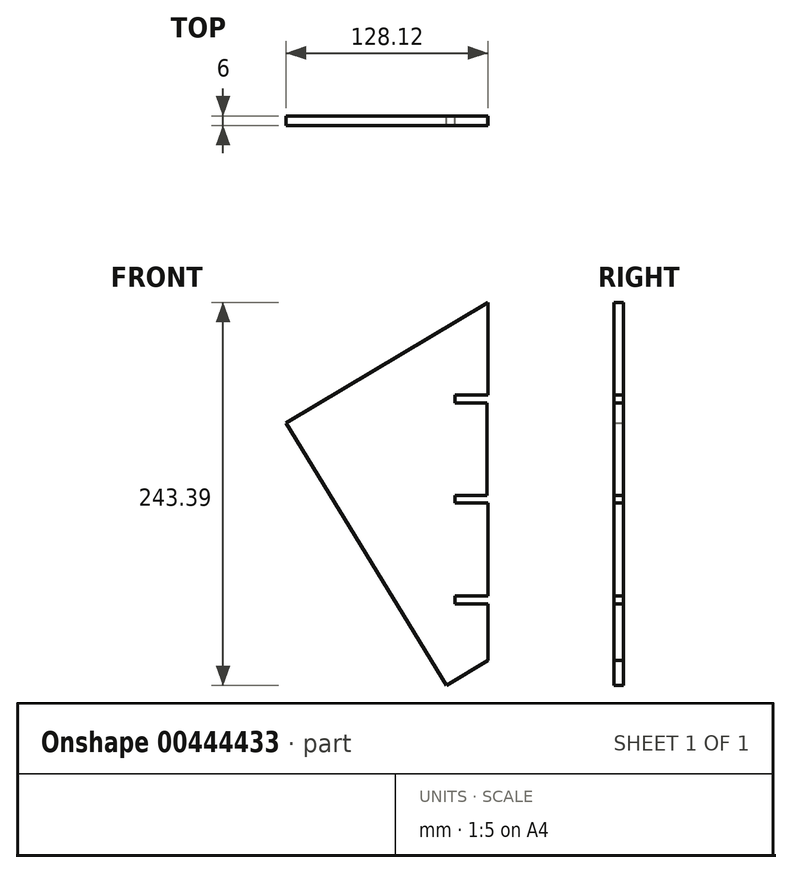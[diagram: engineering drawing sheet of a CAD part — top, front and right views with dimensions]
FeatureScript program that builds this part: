
annotation { "Feature Type Name" : "Feature", "Feature Type Description" : "" }
export const myFeature = defineFeature(function(context is Context, id is Id, definition is map)
    precondition{}
    {
        {
            var Q0;
            Q0=qCreatedBy(makeId("Front.planeOp"),FACE);
            var sketch = newSketch(context, id + "F0", { "sketchPlane" : qUnion([Q0])});
            skLineSegment(sketch, "E0.bottom", {"start": v(0, 58.5) * mm, "end": v(-21, 58.5) * mm});
            skLineSegment(sketch, "E0.top", {"start": v(0, 63.5) * mm, "end": v(-21, 63.5) * mm});
            skLineSegment(sketch, "E0.right", {"start": v(-21, 58.5) * mm, "end": v(-21, 63.5) * mm});
            skLineSegment(sketch, "E1.bottom", {"start": v(0, 122.5) * mm, "end": v(-21, 122.5) * mm});
            skLineSegment(sketch, "E1.top", {"start": v(-0.47, 127.5) * mm, "end": v(-21, 127.5) * mm});
            skLineSegment(sketch, "E1.right", {"start": v(-21, 122.5) * mm, "end": v(-21, 127.5) * mm});
            skLineSegment(sketch, "E2.bottom", {"start": v(-0.47, 186.25) * mm, "end": v(-21, 186.25) * mm});
            skLineSegment(sketch, "E2.top", {"start": v(0, 191.25) * mm, "end": v(-21, 191.25) * mm});
            skLineSegment(sketch, "E2.right", {"start": v(-21, 186.25) * mm, "end": v(-21, 191.25) * mm});
            skLineSegment(sketch, "E3.trimOffspring", {"start": v(0, 191.25) * mm, "end": v(0, 250) * mm});
            skLineSegment(sketch, "E4.trimOffspring", {"start": v(-0.47, 127.5) * mm, "end": v(-0.47, 186.25) * mm});
            skLineSegment(sketch, "E5.trimOffspring", {"start": v(0, 63.75) * mm, "end": v(0, 122.5) * mm});
            skLineSegment(sketch, "E6.trimOffspring", {"start": v(0, 63.5) * mm, "end": v(0, 130.25) * mm});
            skPoint(sketch, "E7.start.orphan", {"position": v(0, 0) * mm});
            skLineSegment(sketch, "E8", {"start": v(-26.33, 6.6) * mm, "end": v(0, 22.68) * mm});
            skLineSegment(sketch, "E9", {"start": v(0, 58.5) * mm, "end": v(0, 22.68) * mm});
            skLineSegment(sketch, "E10", {"start": v(-128.12, 173.38) * mm, "end": v(-26.33, 6.6) * mm});
            skPoint(sketch, "E11.orphan", {"position": v(-37.15, 0) * mm});
            skPoint(sketch, "E12.start.orphan", {"position": v(-108.47, 185.44) * mm});
            skLineSegment(sketch, "E13", {"start": v(0, 250) * mm, "end": v(-128.12, 173.38) * mm});
            skPoint(sketch, "E14.right.end.orphan", {"position": v(-21, 125.25) * mm});
            skPoint(sketch, "E15.top.end.orphan", {"position": v(-21, 93.5) * mm});
            skLineSegment(sketch, "E16", {"start": v(-128.12, 173.38) * mm, "end": v(-0.47, 173.38) * mm});
            skLineSegment(sketch, "E17", {"start": v(-26.33, 6.6) * mm, "end": v(0, 6.6) * mm});
            skSolve(sketch);
        }
        {
            var Q0;
            Q0 = qSketchRegion(id + "F0", true);
            extrude(context, id + "F1", {"entities" : qUnion([Q0]), "depth" : 6 * mm, "offsetDistance" : 25 * mm});
        }
    });
